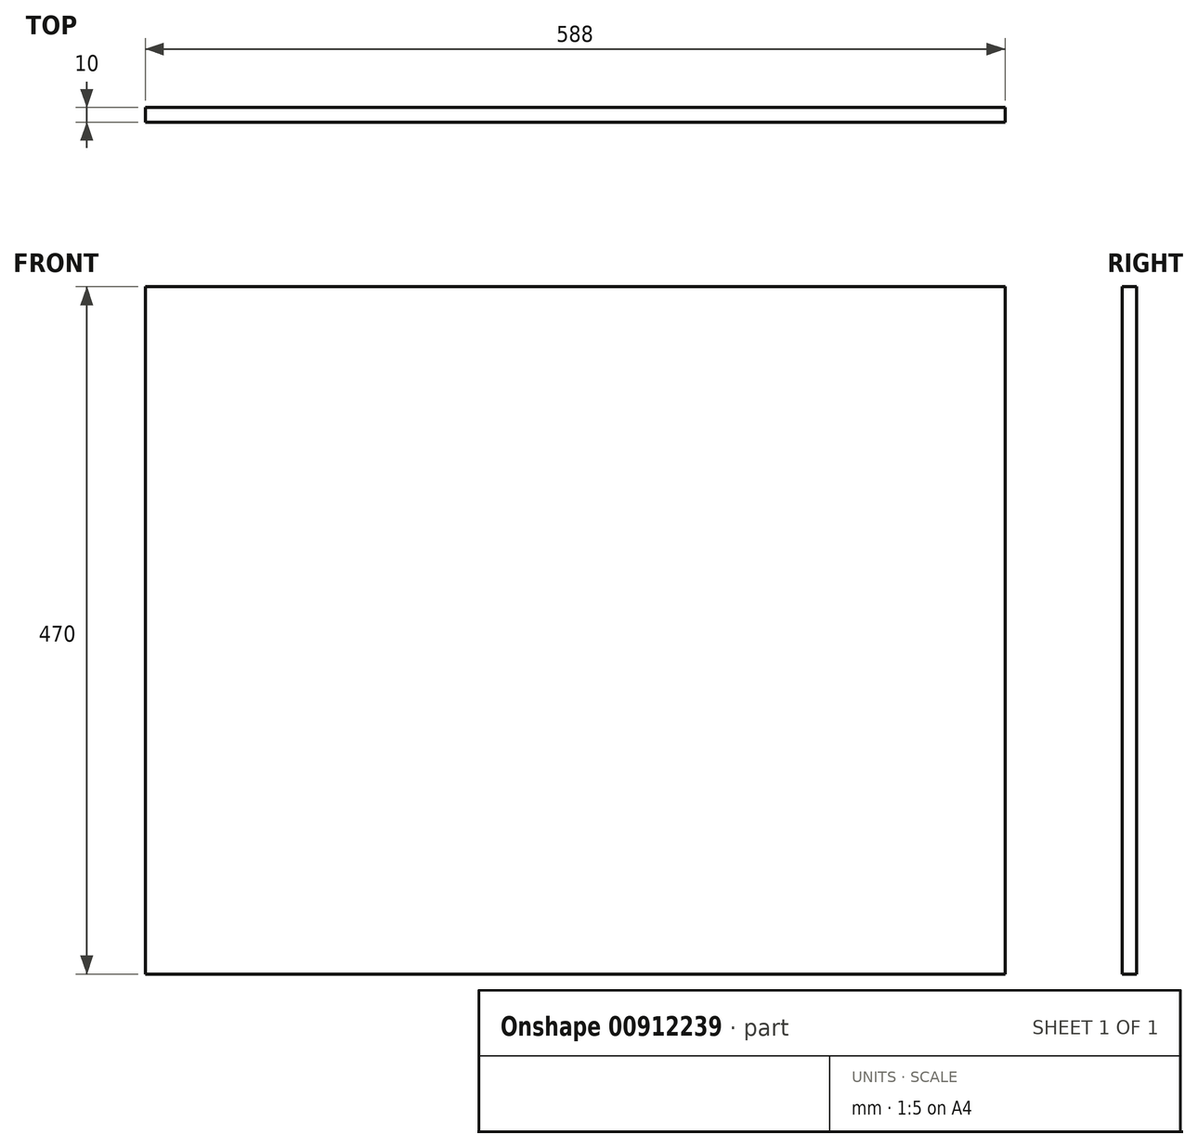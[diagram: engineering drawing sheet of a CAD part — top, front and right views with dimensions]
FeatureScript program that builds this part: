
annotation { "Feature Type Name" : "Feature", "Feature Type Description" : "" }
export const myFeature = defineFeature(function(context is Context, id is Id, definition is map)
    precondition{}
    {
        {
            var Q0;
            Q0=qCreatedBy(makeId("Front.planeOp"),FACE);
            var sketch = newSketch(context, id + "F0", { "sketchPlane" : qUnion([Q0])});
            skLineSegment(sketch, "E0.bottom", {"start": v(-55.8, 441) * mm, "end": v(532.2, 441) * mm});
            skLineSegment(sketch, "E0.top", {"start": v(-55.8, -29) * mm, "end": v(532.2, -29) * mm});
            skLineSegment(sketch, "E0.left", {"start": v(-55.8, 441) * mm, "end": v(-55.8, -29) * mm});
            skLineSegment(sketch, "E0.right", {"start": v(532.2, 441) * mm, "end": v(532.2, -29) * mm});
            skSolve(sketch);
        }
        {
            var Q0;
            Q0=makeQuery(id+"F0.imprint","IMPRINT",FACE,{"disambiguationData":[TD([[makeQuery(id+"F0.imprint","IMPRINT",EDGE,{"derivedFrom":sQuery(id+"F0.wireOp",EDGE,"E0.bottom")}),-1.0]])]});
            extrude(context, id + "F1", {"entities" : qUnion([Q0]), "depth" : 10 * mm, "offsetDistance" : 25 * mm});
        }
    });
